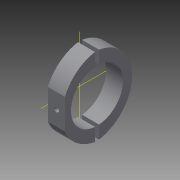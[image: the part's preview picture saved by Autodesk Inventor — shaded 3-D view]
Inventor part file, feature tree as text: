
AUTODESK INVENTOR PART (.ipt)
format: ipt  version: 2015 (Build 190159000, 159)  size: 120,832 bytes
history: native  units: mm
features: sketch x3, extrude x2, projected_geometry x2, hole x1
ambient origin geometry x8: Origin, YZ Plane, XZ Plane, XY Plane, X Axis, Y Axis, Z Axis, Center Point
bodies: Solid1 (feature_tree)
feature tree (8):
  extrude  "Extrusion1"  Depth=26.0mm
  extrude  "Extrusion2"  Depth=33.0mm
  hole  "Hole1"  [1 undecoded]
  sketch  "Sketch1"  dims[d2=13.0mm d6=26.0mm]
  sketch  "Sketch5"  dims[d7=9.0mm d9=33.0mm]
  projected_geometry  "Projected Loop1"
  sketch  "Sketch6"  dims[d10=17.0mm d11=0.0mm d13=6.0mm d14=17.0mm d15=0.0mm d16=5.0mm d17=6.0mm d18=4.0mm d19=2.0mm d20=90.0deg d21=8.0mm d22=20.594885mm]
  projected_geometry  "Projected Loop2"
note: 1 required parameter value undecoded (feature->parameter linkage not recoverable at this tier; creation-order binding heuristic only, values carry confidence <= 0.55)
